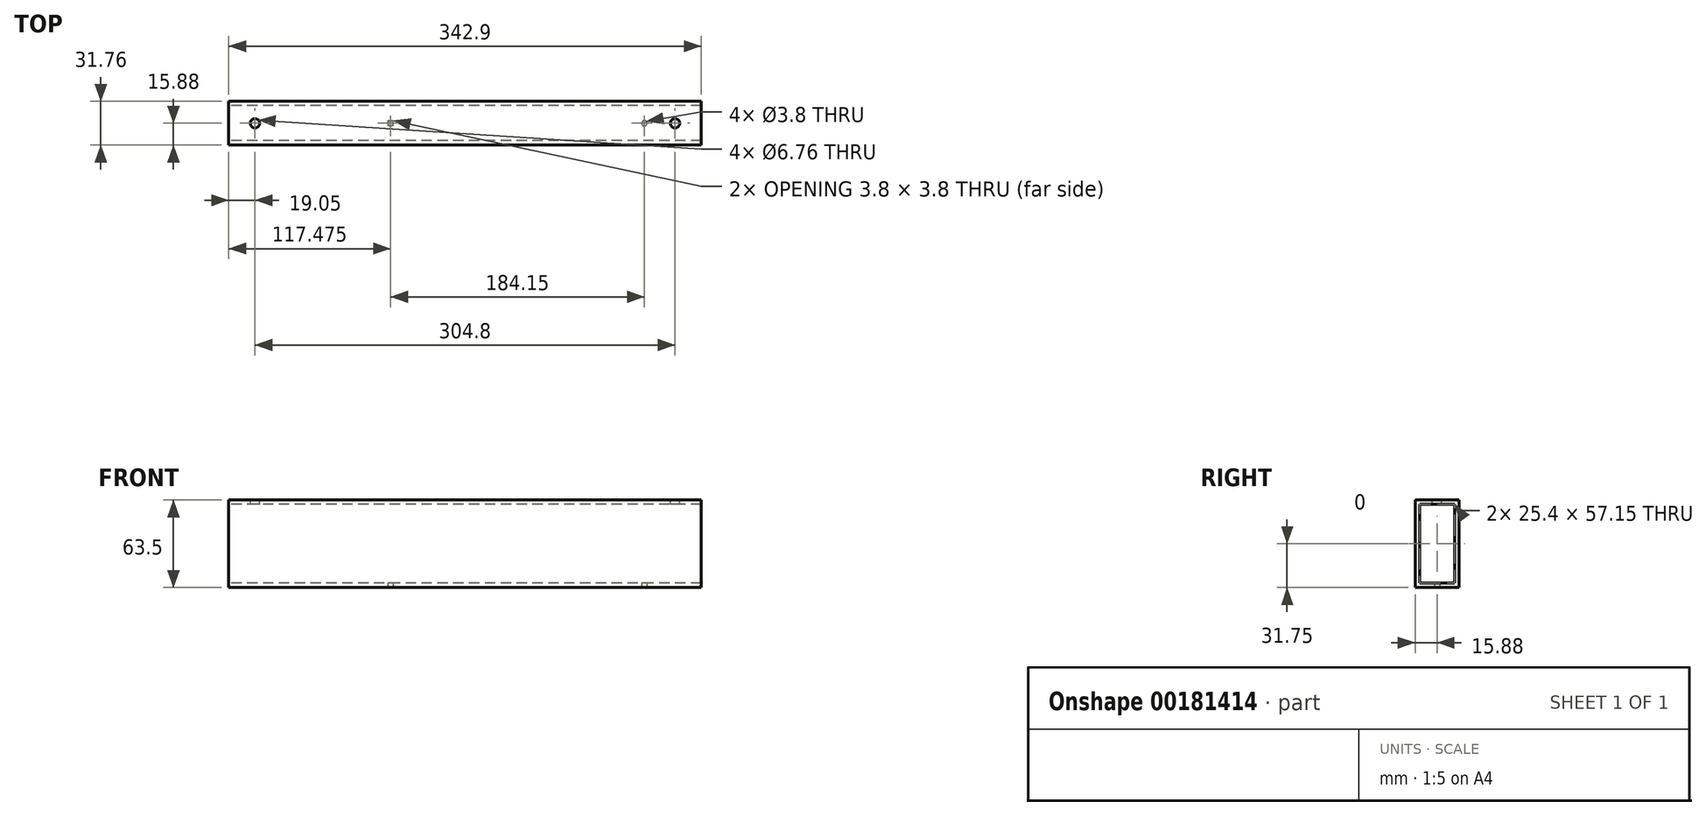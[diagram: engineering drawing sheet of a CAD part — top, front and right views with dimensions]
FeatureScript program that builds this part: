
annotation { "Feature Type Name" : "Feature", "Feature Type Description" : "" }
export const myFeature = defineFeature(function(context is Context, id is Id, definition is map)
    precondition{}
    {
        {
            var Q0;
            Q0=qCreatedBy(makeId("Right.planeOp"),FACE);
            var sketch = newSketch(context, id + "F0", { "sketchPlane" : qUnion([Q0])});
            skLineSegment(sketch, "E0.bottom", {"start": v(-15.87, 31.75) * mm, "end": v(15.88, 31.75) * mm});
            skLineSegment(sketch, "E0.top", {"start": v(-15.88, -31.75) * mm, "end": v(15.88, -31.75) * mm});
            skLineSegment(sketch, "E0.left", {"start": v(-15.87, 31.75) * mm, "end": v(-15.88, -31.75) * mm});
            skLineSegment(sketch, "E0.right", {"start": v(15.88, 31.75) * mm, "end": v(15.87, -31.75) * mm});
            skLineSegment(sketch, "E1.bottom", {"start": v(-12.7, 28.58) * mm, "end": v(12.7, 28.58) * mm});
            skLineSegment(sketch, "E1.top", {"start": v(-12.7, -28.58) * mm, "end": v(12.7, -28.58) * mm});
            skLineSegment(sketch, "E1.left", {"start": v(-12.7, 28.58) * mm, "end": v(-12.7, -28.58) * mm});
            skLineSegment(sketch, "E1.right", {"start": v(12.7, 28.58) * mm, "end": v(12.7, -28.58) * mm});
            skLineSegment(sketch, "E2", {"start": v(-12.7, 28.58) * mm, "end": v(12.7, -28.57) * mm, "construction": true});
            skSolve(sketch);
        }
        {
            var Q0;
            Q0=makeQuery(id+"F0.imprint","IMPRINT",FACE,{"disambiguationData":[TD([[makeQuery(id+"F0.imprint","IMPRINT",EDGE,{"derivedFrom":sQuery(id+"F0.wireOp",EDGE,"E0.bottom")}),-1.0]])]});
            extrude(context, id + "F1", {"entities" : qUnion([Q0]), "depth" : 342.9 * mm});
        }
        {
            var Q0;
            Q0=makeQuery(id+"F1.opExtrude","SWEPT_FACE",FACE,{"disambiguationData":[OSD([sQuery(id+"F0.wireOp",EDGE,"E0.top")])]});
            var sketch = newSketch(context, id + "F2", { "sketchPlane" : qUnion([Q0])});
            skLineSegment(sketch, "E3", {"start": v(0, 0) * mm, "end": v(342.9, 0) * mm, "construction": true});
            skLineSegment(sketch, "E4", {"start": v(117.48, 15.88) * mm, "end": v(117.48, -15.87) * mm, "construction": true});
            skLineSegment(sketch, "E5", {"start": v(301.63, 15.88) * mm, "end": v(301.63, -15.87) * mm, "construction": true});
            skCircle(sketch, "E6", {"center": v(117.48, 0) * mm, "radius": 1.9 * mm});
            skCircle(sketch, "E7", {"center": v(301.63, 0) * mm, "radius": 1.9 * mm});
            skSolve(sketch);
        }
        {
            var Q0;
            Q0=makeQuery(id+"F2.imprint","IMPRINT",FACE,{"disambiguationData":[TD([[makeQuery(id+"F2.imprint","IMPRINT",EDGE,{"derivedFrom":sQuery(id+"F2.wireOp",EDGE,"E6")}),1.0]])]});
            var Q1;
            Q1=makeQuery(id+"F2.imprint","IMPRINT",FACE,{"disambiguationData":[TD([[makeQuery(id+"F2.imprint","IMPRINT",EDGE,{"derivedFrom":sQuery(id+"F2.wireOp",EDGE,"E7")}),1.0]])]});
            extrude(context, id + "F3", {"entities" : qUnion([Q0, Q1]), "operationType" : NewBodyOperationType.REMOVE, "endBound" : BoundingType.UP_TO_NEXT, "oppositeDirection" : true, "depth" : 25.4 * mm});
        }
        {
            var Q0;
            Q0=makeQuery(id+"F1.opExtrude","SWEPT_FACE",FACE,{"disambiguationData":[OSD([sQuery(id+"F0.wireOp",EDGE,"E0.bottom")])]});
            var sketch = newSketch(context, id + "F4", { "sketchPlane" : qUnion([Q0])});
            skLineSegment(sketch, "E8", {"start": v(0, 0) * mm, "end": v(342.9, 0) * mm, "construction": true});
            skLineSegment(sketch, "E9", {"start": v(19.05, 15.88) * mm, "end": v(19.05, -15.87) * mm, "construction": true});
            skLineSegment(sketch, "E10", {"start": v(323.85, 15.88) * mm, "end": v(323.85, -15.87) * mm, "construction": true});
            skCircle(sketch, "E11", {"center": v(19.05, 0) * mm, "radius": 3.38 * mm});
            skCircle(sketch, "E12", {"center": v(323.85, 0) * mm, "radius": 3.38 * mm});
            skSolve(sketch);
        }
        {
            var Q0;
            Q0=makeQuery(id+"F4.imprint","IMPRINT",FACE,{"disambiguationData":[TD([[makeQuery(id+"F4.imprint","IMPRINT",EDGE,{"derivedFrom":sQuery(id+"F4.wireOp",EDGE,"E11")}),1.0]])]});
            var Q1;
            Q1=makeQuery(id+"F4.imprint","IMPRINT",FACE,{"disambiguationData":[TD([[makeQuery(id+"F4.imprint","IMPRINT",EDGE,{"derivedFrom":sQuery(id+"F4.wireOp",EDGE,"E12")}),1.0]])]});
            extrude(context, id + "F5", {"entities" : qUnion([Q0, Q1]), "operationType" : NewBodyOperationType.REMOVE, "endBound" : BoundingType.UP_TO_NEXT, "oppositeDirection" : true, "depth" : 25.4 * mm});
        }
        {
            var Q0;
            Q0=makeQuery(id+"F1.opExtrude","SWEPT_BODY",BODY,{"disambiguationData":[OSD([sQuery(id+"F0.wireOp",EDGE,"E0.bottom"),sQuery(id+"F0.wireOp",EDGE,"E0.top"),sQuery(id+"F0.wireOp",EDGE,"E0.left"),sQuery(id+"F0.wireOp",EDGE,"E0.right"),sQuery(id+"F0.wireOp",EDGE,"E1.bottom"),sQuery(id+"F0.wireOp",EDGE,"E1.top"),sQuery(id+"F0.wireOp",EDGE,"E1.left"),sQuery(id+"F0.wireOp",EDGE,"E1.right")])]});
            transform(context, id + "F6", {"entities" : qUnion([Q0]), "transformType" : TransformType.TRANSLATION_3D, "dx" : 0 * mm, "dy" : 0 * mm, "dz" : 0 * mm, "makeCopy" : true});
        }
    });
